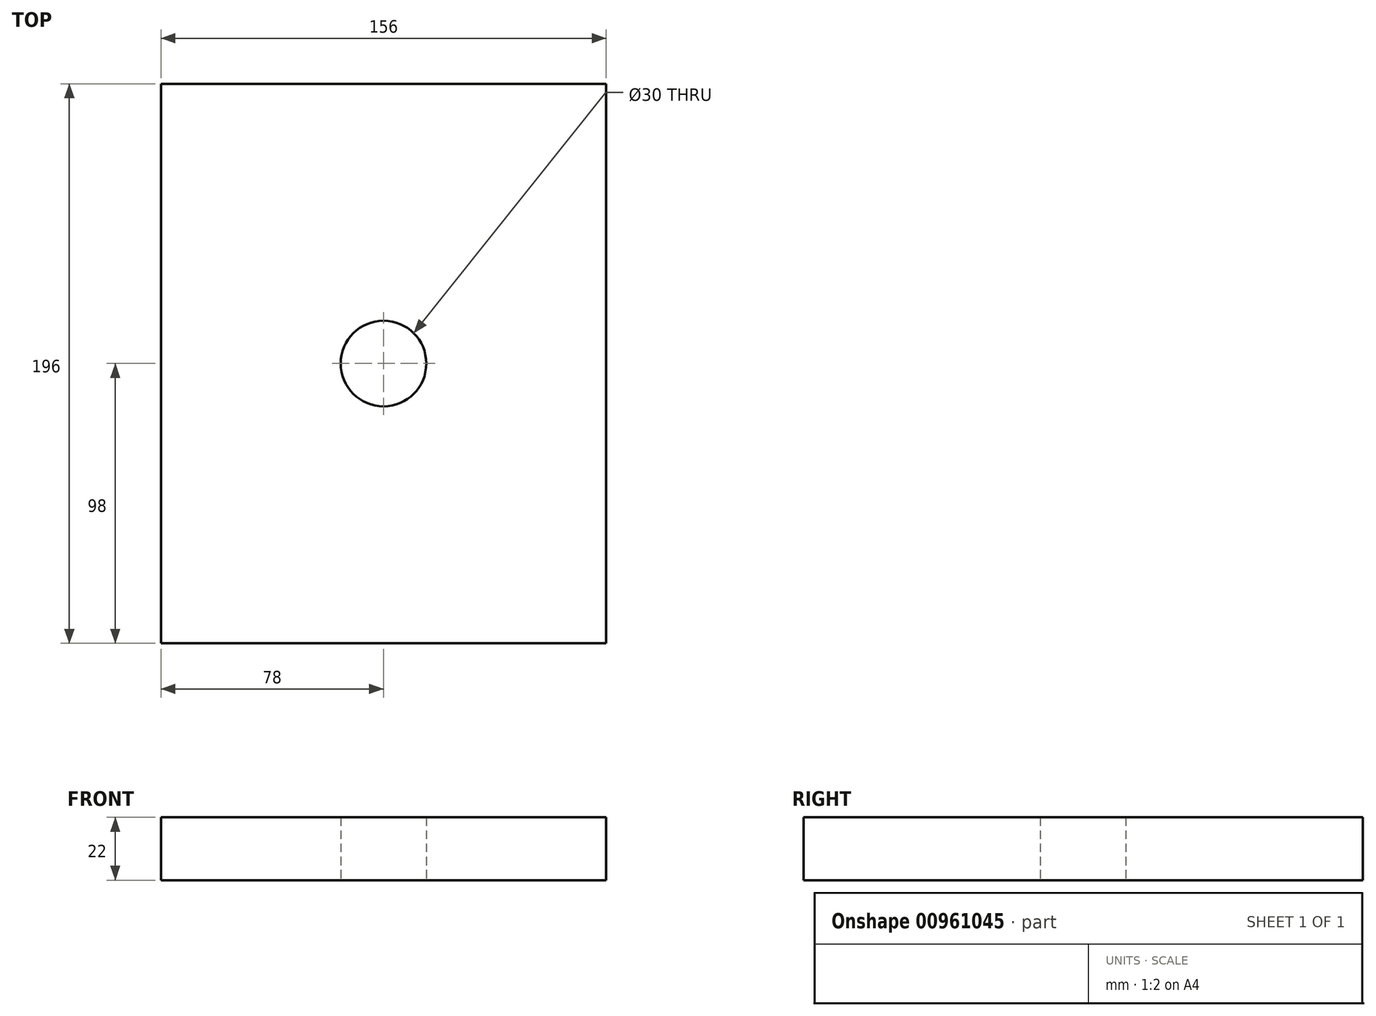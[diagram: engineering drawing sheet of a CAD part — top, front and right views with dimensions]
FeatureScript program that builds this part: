
annotation { "Feature Type Name" : "Feature", "Feature Type Description" : "" }
export const myFeature = defineFeature(function(context is Context, id is Id, definition is map)
    precondition{}
    {
        {
            var Q0;
            Q0=qCreatedBy(makeId("Top.planeOp"),FACE);
            var sketch = newSketch(context, id + "F0", { "sketchPlane" : qUnion([Q0])});
            skLineSegment(sketch, "E0.bottom", {"start": v(-78, 98) * mm, "end": v(78, 98) * mm});
            skLineSegment(sketch, "E0.top", {"start": v(-78, -98) * mm, "end": v(78, -98) * mm});
            skLineSegment(sketch, "E0.left", {"start": v(-78, 98) * mm, "end": v(-78, -98) * mm});
            skLineSegment(sketch, "E0.right", {"start": v(78, 98) * mm, "end": v(78, -98) * mm});
            skLineSegment(sketch, "E1", {"start": v(0, 98) * mm, "end": v(0, -98) * mm, "construction": true});
            skCircle(sketch, "E2", {"center": v(0, 0) * mm, "radius": 15 * mm});
            skSolve(sketch);
        }
        {
            var Q0;
            Q0=makeQuery(id+"F0.imprint","IMPRINT",FACE,{"disambiguationData":[TD([[makeQuery(id+"F0.imprint","IMPRINT",EDGE,{"derivedFrom":sQuery(id+"F0.wireOp",EDGE,"E0.bottom")}),-1.0]])]});
            extrude(context, id + "F1", {"entities" : qUnion([Q0]), "depth" : 22 * mm, "offsetDistance" : 25 * mm});
        }
    });
